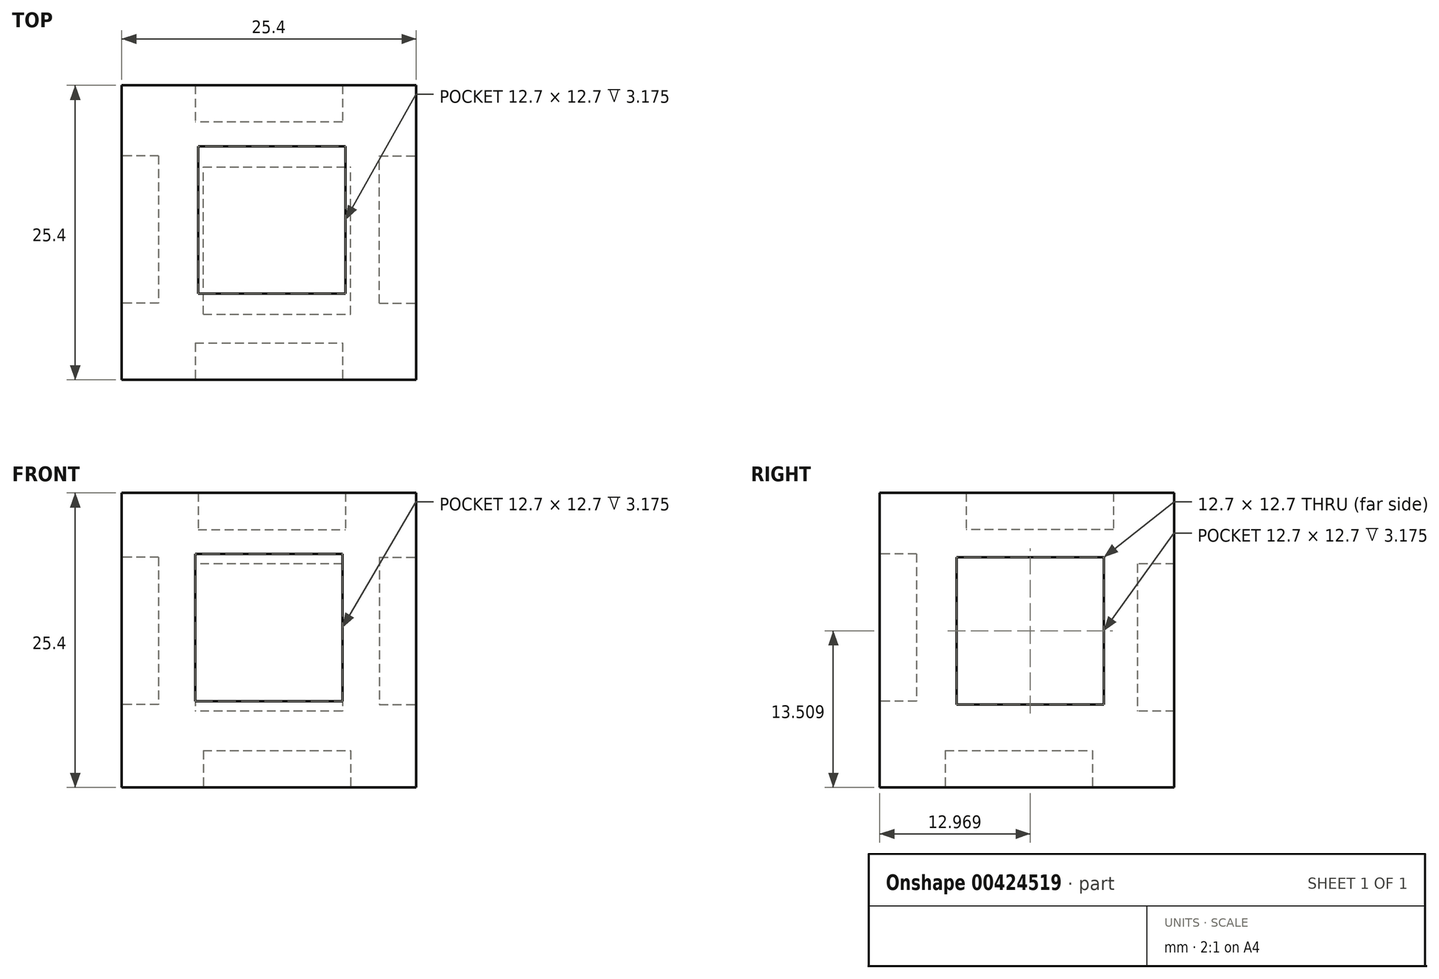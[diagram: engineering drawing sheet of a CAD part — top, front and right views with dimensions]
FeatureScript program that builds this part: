
annotation { "Feature Type Name" : "Feature", "Feature Type Description" : "" }
export const myFeature = defineFeature(function(context is Context, id is Id, definition is map)
    precondition{}
    {
        {
            var Q0;
            Q0=qCreatedBy(makeId("Top.planeOp"),FACE);
            var sketch = newSketch(context, id + "F0", { "sketchPlane" : qUnion([Q0])});
            skLineSegment(sketch, "E0.bottom", {"start": v(-12.95, 8.42) * mm, "end": v(12.45, 8.42) * mm});
            skLineSegment(sketch, "E0.top", {"start": v(-12.95, -16.98) * mm, "end": v(12.45, -16.98) * mm});
            skLineSegment(sketch, "E0.left", {"start": v(-12.95, 8.42) * mm, "end": v(-12.95, -16.98) * mm});
            skLineSegment(sketch, "E0.right", {"start": v(12.45, 8.42) * mm, "end": v(12.45, -16.98) * mm});
            skSolve(sketch);
        }
        {
            var Q0;
            Q0 = qSketchRegion(id + "F0", true);
            extrude(context, id + "F1", {"entities" : qUnion([Q0]), "depth" : 25.4 * mm});
        }
        {
            var Q0;
            Q0=makeQuery(id+"F1.opExtrude","SWEPT_FACE",FACE,{"disambiguationData":[OSD([sQuery(id+"F0.wireOp",EDGE,"E0.top")])]});
            var sketch = newSketch(context, id + "F2", { "sketchPlane" : qUnion([Q0])});
            skLineSegment(sketch, "E1.bottom", {"start": v(-6.62, 20.15) * mm, "end": v(6.08, 20.15) * mm});
            skLineSegment(sketch, "E1.top", {"start": v(-6.62, 7.45) * mm, "end": v(6.08, 7.45) * mm});
            skLineSegment(sketch, "E1.left", {"start": v(-6.62, 20.15) * mm, "end": v(-6.62, 7.45) * mm});
            skLineSegment(sketch, "E1.right", {"start": v(6.08, 20.15) * mm, "end": v(6.08, 7.45) * mm});
            skSolve(sketch);
        }
        {
            var Q0;
            Q0=makeQuery(id+"F2.imprint","IMPRINT",FACE,{"disambiguationData":[TD([[makeQuery(id+"F2.imprint","IMPRINT",EDGE,{"derivedFrom":sQuery(id+"F2.wireOp",EDGE,"E1.bottom")}),-1.0]])]});
            extrude(context, id + "F3", {"entities" : qUnion([Q0]), "operationType" : NewBodyOperationType.REMOVE, "oppositeDirection" : true, "depth" : 3.17 * mm});
        }
        {
            var Q0;
            Q0=makeQuery(id+"F1.opExtrude","SWEPT_FACE",FACE,{"disambiguationData":[OSD([sQuery(id+"F0.wireOp",EDGE,"E0.left")])]});
            var sketch = newSketch(context, id + "F4", { "sketchPlane" : qUnion([Q0])});
            skLineSegment(sketch, "E2.bottom", {"start": v(-2.34, 19.86) * mm, "end": v(10.36, 19.86) * mm});
            skLineSegment(sketch, "E2.top", {"start": v(-2.34, 7.16) * mm, "end": v(10.36, 7.16) * mm});
            skLineSegment(sketch, "E2.left", {"start": v(-2.34, 19.86) * mm, "end": v(-2.34, 7.16) * mm});
            skLineSegment(sketch, "E2.right", {"start": v(10.36, 19.86) * mm, "end": v(10.36, 7.16) * mm});
            skSolve(sketch);
        }
        {
            var Q0;
            Q0=makeQuery(id+"F4.imprint","IMPRINT",FACE,{"disambiguationData":[TD([[makeQuery(id+"F4.imprint","IMPRINT",EDGE,{"derivedFrom":sQuery(id+"F4.wireOp",EDGE,"E2.bottom")}),-1.0]])]});
            extrude(context, id + "F5", {"entities" : qUnion([Q0]), "operationType" : NewBodyOperationType.REMOVE, "oppositeDirection" : true, "depth" : 3.17 * mm});
        }
        {
            var Q0;
            Q0=makeQuery(id+"F1.opExtrude","SWEPT_FACE",FACE,{"disambiguationData":[OSD([sQuery(id+"F0.wireOp",EDGE,"E0.bottom")])]});
            var sketch = newSketch(context, id + "F6", { "sketchPlane" : qUnion([Q0])});
            skLineSegment(sketch, "E3.bottom", {"start": v(-6.08, 19.28) * mm, "end": v(6.62, 19.28) * mm});
            skLineSegment(sketch, "E3.top", {"start": v(-6.08, 6.58) * mm, "end": v(6.62, 6.58) * mm});
            skLineSegment(sketch, "E3.left", {"start": v(-6.08, 19.28) * mm, "end": v(-6.08, 6.58) * mm});
            skLineSegment(sketch, "E3.right", {"start": v(6.62, 19.28) * mm, "end": v(6.62, 6.58) * mm});
            skSolve(sketch);
        }
        {
            var Q0;
            Q0 = qSketchRegion(id + "F6", true);
            extrude(context, id + "F7", {"entities" : qUnion([Q0]), "operationType" : NewBodyOperationType.REMOVE, "oppositeDirection" : true, "depth" : 3.17 * mm});
        }
        {
            var Q0;
            Q0=makeQuery(id+"F1.opExtrude","SWEPT_FACE",FACE,{"disambiguationData":[OSD([sQuery(id+"F0.wireOp",EDGE,"E0.right")])]});
            var sketch = newSketch(context, id + "F8", { "sketchPlane" : qUnion([Q0])});
            skLineSegment(sketch, "E4.bottom", {"start": v(-10.36, 19.86) * mm, "end": v(2.34, 19.86) * mm});
            skLineSegment(sketch, "E4.top", {"start": v(-10.36, 7.16) * mm, "end": v(2.34, 7.16) * mm});
            skLineSegment(sketch, "E4.left", {"start": v(-10.36, 19.86) * mm, "end": v(-10.36, 7.16) * mm});
            skLineSegment(sketch, "E4.right", {"start": v(2.34, 19.86) * mm, "end": v(2.34, 7.16) * mm});
            skSolve(sketch);
        }
        {
            var Q0;
            Q0 = qSketchRegion(id + "F8", true);
            extrude(context, id + "F9", {"entities" : qUnion([Q0]), "operationType" : NewBodyOperationType.REMOVE, "oppositeDirection" : true, "depth" : 3.17 * mm});
        }
        {
            var Q0;
            Q0=makeQuery(id+"F1.opExtrude","CAP_FACE",FACE,{"disambiguationData":[OSD([sQuery(id+"F0.wireOp",EDGE,"E0.bottom"),sQuery(id+"F0.wireOp",EDGE,"E0.top"),sQuery(id+"F0.wireOp",EDGE,"E0.left"),sQuery(id+"F0.wireOp",EDGE,"E0.right")])],"isStart":false});
            var sketch = newSketch(context, id + "F10", { "sketchPlane" : qUnion([Q0])});
            skLineSegment(sketch, "E5.bottom", {"start": v(-6.37, 3.17) * mm, "end": v(6.33, 3.17) * mm});
            skLineSegment(sketch, "E5.top", {"start": v(-6.37, -9.53) * mm, "end": v(6.33, -9.53) * mm});
            skLineSegment(sketch, "E5.left", {"start": v(-6.37, 3.17) * mm, "end": v(-6.37, -9.53) * mm});
            skLineSegment(sketch, "E5.right", {"start": v(6.33, 3.17) * mm, "end": v(6.33, -9.53) * mm});
            skSolve(sketch);
        }
        {
            var Q0;
            Q0 = qSketchRegion(id + "F10", true);
            extrude(context, id + "F11", {"entities" : qUnion([Q0]), "operationType" : NewBodyOperationType.REMOVE, "oppositeDirection" : true, "depth" : 3.17 * mm});
        }
        {
            var Q0;
            Q0=makeQuery(id+"F1.opExtrude","CAP_FACE",FACE,{"disambiguationData":[OSD([sQuery(id+"F0.wireOp",EDGE,"E0.bottom"),sQuery(id+"F0.wireOp",EDGE,"E0.top"),sQuery(id+"F0.wireOp",EDGE,"E0.left"),sQuery(id+"F0.wireOp",EDGE,"E0.right")])],"isStart":true});
            var sketch = newSketch(context, id + "F12", { "sketchPlane" : qUnion([Q0])});
            skLineSegment(sketch, "E6.bottom", {"start": v(-5.92, 11.33) * mm, "end": v(6.78, 11.33) * mm});
            skLineSegment(sketch, "E6.top", {"start": v(-5.92, -1.37) * mm, "end": v(6.78, -1.37) * mm});
            skLineSegment(sketch, "E6.left", {"start": v(-5.92, 11.33) * mm, "end": v(-5.92, -1.37) * mm});
            skLineSegment(sketch, "E6.right", {"start": v(6.78, 11.33) * mm, "end": v(6.78, -1.37) * mm});
            skSolve(sketch);
        }
        {
            var Q0;
            Q0 = qSketchRegion(id + "F12", true);
            extrude(context, id + "F13", {"entities" : qUnion([Q0]), "operationType" : NewBodyOperationType.REMOVE, "oppositeDirection" : true, "depth" : 3.17 * mm});
        }
        {
            var Q0;
            Q0=makeQuery(id+"F11.boolean.opBoolean","COPY",FACE,{"derivedFrom":makeQuery(id+"F11.opExtrude","CAP_FACE",FACE,{"disambiguationData":[OSD([sQuery(id+"F10.wireOp",EDGE,"E5.bottom"),sQuery(id+"F10.wireOp",EDGE,"E5.top"),sQuery(id+"F10.wireOp",EDGE,"E5.left"),sQuery(id+"F10.wireOp",EDGE,"E5.right")])],"isStart":false})});
            var sketch = newSketch(context, id + "F14", { "sketchPlane" : qUnion([Q0])});
            skLineSegment(sketch, "E7.bottom", {"start": v(-6.37, 3.17) * mm, "end": v(6.33, 3.17) * mm});
            skLineSegment(sketch, "E7.top", {"start": v(-6.37, -9.53) * mm, "end": v(6.33, -9.53) * mm});
            skLineSegment(sketch, "E7.left", {"start": v(-6.37, 3.17) * mm, "end": v(-6.37, -9.53) * mm});
            skLineSegment(sketch, "E7.right", {"start": v(6.33, 3.17) * mm, "end": v(6.33, -9.53) * mm});
            skSolve(sketch);
        }
        {
            var Q0;
            Q0 = qSketchRegion(id + "F14", true);
            extrude(context, id + "F15", {"entities" : qUnion([Q0]), "depth" : 3.17 * mm});
        }
        {
            var Q0;
            Q0=makeQuery(id+"F7.boolean.opBoolean","COPY",FACE,{"derivedFrom":makeQuery(id+"F7.opExtrude","CAP_FACE",FACE,{"disambiguationData":[OSD([sQuery(id+"F6.wireOp",EDGE,"E3.bottom"),sQuery(id+"F6.wireOp",EDGE,"E3.top"),sQuery(id+"F6.wireOp",EDGE,"E3.left"),sQuery(id+"F6.wireOp",EDGE,"E3.right")])],"isStart":false})});
            var sketch = newSketch(context, id + "F16", { "sketchPlane" : qUnion([Q0])});
            skLineSegment(sketch, "E8.bottom", {"start": v(-6.08, 19.28) * mm, "end": v(6.62, 19.28) * mm});
            skLineSegment(sketch, "E8.top", {"start": v(-6.08, 6.58) * mm, "end": v(6.62, 6.58) * mm});
            skLineSegment(sketch, "E8.left", {"start": v(-6.08, 19.28) * mm, "end": v(-6.08, 6.58) * mm});
            skLineSegment(sketch, "E8.right", {"start": v(6.62, 19.28) * mm, "end": v(6.62, 6.58) * mm});
            skSolve(sketch);
        }
        {
            var Q0;
            Q0 = qSketchRegion(id + "F16", true);
            extrude(context, id + "F17", {"entities" : qUnion([Q0]), "depth" : 3.17 * mm});
        }
        {
            var Q0;
            Q0=makeQuery(id+"F5.boolean.opBoolean","COPY",FACE,{"derivedFrom":makeQuery(id+"F5.opExtrude","CAP_FACE",FACE,{"disambiguationData":[OSD([sQuery(id+"F4.wireOp",EDGE,"E2.bottom"),sQuery(id+"F4.wireOp",EDGE,"E2.top"),sQuery(id+"F4.wireOp",EDGE,"E2.left"),sQuery(id+"F4.wireOp",EDGE,"E2.right")])],"isStart":false})});
            var sketch = newSketch(context, id + "F18", { "sketchPlane" : qUnion([Q0])});
            skLineSegment(sketch, "E9.bottom", {"start": v(-2.34, 19.86) * mm, "end": v(10.36, 19.86) * mm});
            skLineSegment(sketch, "E9.top", {"start": v(-2.34, 7.16) * mm, "end": v(10.36, 7.16) * mm});
            skLineSegment(sketch, "E9.left", {"start": v(-2.34, 19.86) * mm, "end": v(-2.34, 7.16) * mm});
            skLineSegment(sketch, "E9.right", {"start": v(10.36, 19.86) * mm, "end": v(10.36, 7.16) * mm});
            skSolve(sketch);
        }
        {
            var Q0;
            Q0 = qSketchRegion(id + "F18", true);
            extrude(context, id + "F19", {"entities" : qUnion([Q0]), "depth" : 3.17 * mm});
        }
        {
            var Q0;
            Q0=makeQuery(id+"F9.boolean.opBoolean","COPY",FACE,{"derivedFrom":makeQuery(id+"F9.opExtrude","CAP_FACE",FACE,{"disambiguationData":[OSD([sQuery(id+"F8.wireOp",EDGE,"E4.bottom"),sQuery(id+"F8.wireOp",EDGE,"E4.top"),sQuery(id+"F8.wireOp",EDGE,"E4.left"),sQuery(id+"F8.wireOp",EDGE,"E4.right")])],"isStart":false})});
            var sketch = newSketch(context, id + "F20", { "sketchPlane" : qUnion([Q0])});
            skLineSegment(sketch, "E10.bottom", {"start": v(-10.36, 19.86) * mm, "end": v(2.34, 19.86) * mm});
            skLineSegment(sketch, "E10.top", {"start": v(-10.36, 7.16) * mm, "end": v(2.34, 7.16) * mm});
            skLineSegment(sketch, "E10.left", {"start": v(-10.36, 19.86) * mm, "end": v(-10.36, 7.16) * mm});
            skLineSegment(sketch, "E10.right", {"start": v(2.34, 19.86) * mm, "end": v(2.34, 7.16) * mm});
            skSolve(sketch);
        }
        {
            var Q0;
            Q0 = qSketchRegion(id + "F20", true);
            extrude(context, id + "F21", {"entities" : qUnion([Q0]), "depth" : 3.17 * mm});
        }
        {
            var Q0;
            Q0=makeQuery(id+"F3.boolean.opBoolean","COPY",FACE,{"derivedFrom":makeQuery(id+"F3.opExtrude","CAP_FACE",FACE,{"disambiguationData":[OSD([sQuery(id+"F2.wireOp",EDGE,"E1.bottom"),sQuery(id+"F2.wireOp",EDGE,"E1.top"),sQuery(id+"F2.wireOp",EDGE,"E1.left"),sQuery(id+"F2.wireOp",EDGE,"E1.right")])],"isStart":false})});
            var sketch = newSketch(context, id + "F22", { "sketchPlane" : qUnion([Q0])});
            skLineSegment(sketch, "E11.bottom", {"start": v(-6.62, 20.15) * mm, "end": v(6.08, 20.15) * mm});
            skLineSegment(sketch, "E11.top", {"start": v(-6.62, 7.45) * mm, "end": v(6.08, 7.45) * mm});
            skLineSegment(sketch, "E11.left", {"start": v(-6.62, 20.15) * mm, "end": v(-6.62, 7.45) * mm});
            skLineSegment(sketch, "E11.right", {"start": v(6.08, 20.15) * mm, "end": v(6.08, 7.45) * mm});
            skSolve(sketch);
        }
        {
            var Q0;
            Q0 = qSketchRegion(id + "F22", true);
            extrude(context, id + "F23", {"entities" : qUnion([Q0]), "depth" : 3.17 * mm});
        }
        {
            var Q0;
            Q0=makeQuery(id+"F13.boolean.opBoolean","COPY",FACE,{"derivedFrom":makeQuery(id+"F13.opExtrude","CAP_FACE",FACE,{"disambiguationData":[OSD([sQuery(id+"F12.wireOp",EDGE,"E6.bottom"),sQuery(id+"F12.wireOp",EDGE,"E6.top"),sQuery(id+"F12.wireOp",EDGE,"E6.left"),sQuery(id+"F12.wireOp",EDGE,"E6.right")])],"isStart":false})});
            var sketch = newSketch(context, id + "F24", { "sketchPlane" : qUnion([Q0])});
            skLineSegment(sketch, "E12.bottom", {"start": v(-5.92, 11.33) * mm, "end": v(6.78, 11.33) * mm});
            skLineSegment(sketch, "E12.top", {"start": v(-5.92, -1.37) * mm, "end": v(6.78, -1.37) * mm});
            skLineSegment(sketch, "E12.left", {"start": v(-5.92, 11.33) * mm, "end": v(-5.92, -1.37) * mm});
            skLineSegment(sketch, "E12.right", {"start": v(6.78, 11.33) * mm, "end": v(6.78, -1.37) * mm});
            skSolve(sketch);
        }
        {
            var Q0;
            Q0 = qSketchRegion(id + "F24", true);
            extrude(context, id + "F25", {"entities" : qUnion([Q0]), "depth" : 3.17 * mm});
        }
    });
